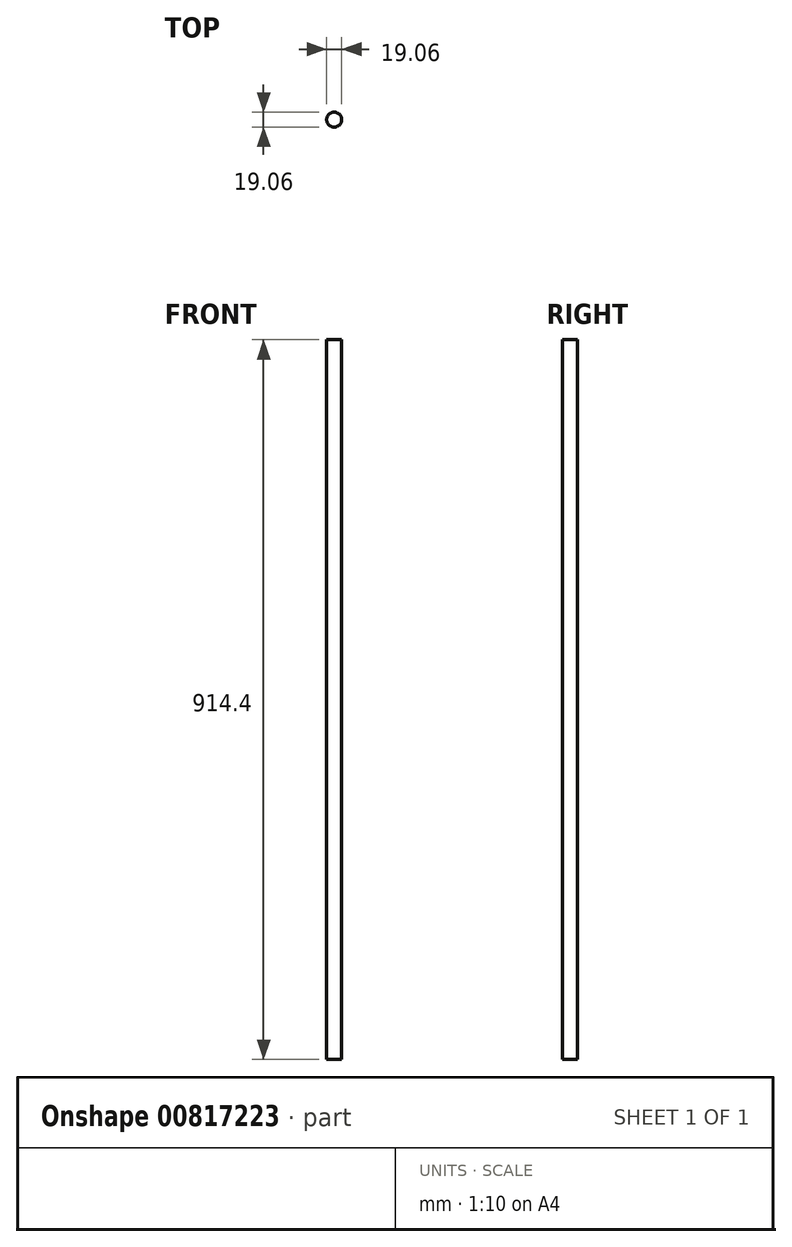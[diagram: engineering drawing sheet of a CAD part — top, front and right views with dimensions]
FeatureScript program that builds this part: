
annotation { "Feature Type Name" : "Feature", "Feature Type Description" : "" }
export const myFeature = defineFeature(function(context is Context, id is Id, definition is map)
    precondition{}
    {
        {
            var Q0;
            Q0=qCreatedBy(makeId("Top.planeOp"),FACE);
            var sketch = newSketch(context, id + "F0", { "sketchPlane" : qUnion([Q0])});
            skCircle(sketch, "E0", {"center": v(0, 0) * mm, "radius": 9.53 * mm});
            skSolve(sketch);
        }
        {
            var Q0;
            Q0=sQuery(id+"F0.wireOp",EDGE,"E0");
            extrude(context, id + "F1", {"bodyType" : ToolBodyType.SURFACE, "surfaceEntities" : qUnion([Q0]), "depth" : 914.4 * mm, "offsetDistance" : 25.4 * mm});
        }
    });
